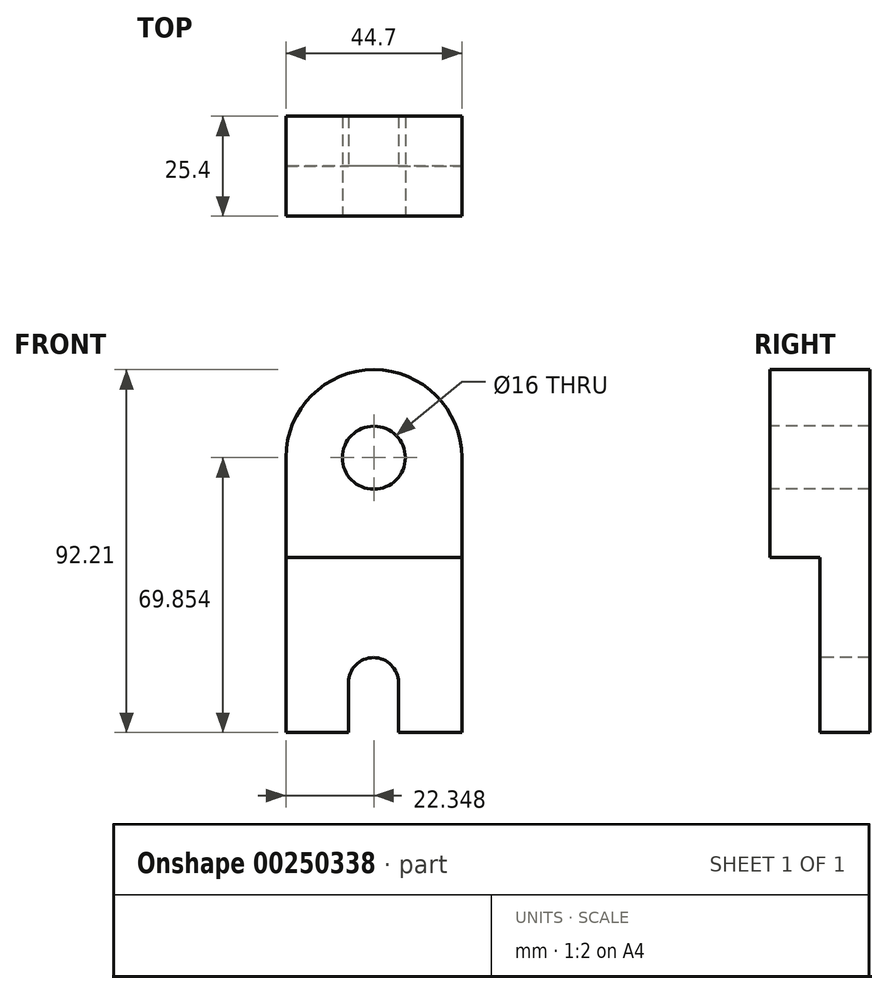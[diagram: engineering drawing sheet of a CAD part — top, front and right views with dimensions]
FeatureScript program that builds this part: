
annotation { "Feature Type Name" : "Feature", "Feature Type Description" : "" }
export const myFeature = defineFeature(function(context is Context, id is Id, definition is map)
    precondition{}
    {
        {
            var Q0;
            Q0=qCreatedBy(makeId("Front.planeOp"),FACE);
            var sketch = newSketch(context, id + "F0", { "sketchPlane" : qUnion([Q0])});
            skLineSegment(sketch, "E0", {"start": v(-44.7, -31.42) * mm, "end": v(-44.7, 38.43) * mm});
            skLineSegment(sketch, "E1", {"start": v(-44.7, -31.42) * mm, "end": v(0, -31.42) * mm});
            skLineSegment(sketch, "E2", {"start": v(0, -31.42) * mm, "end": v(0, 38.43) * mm});
            skArc(sketch, "E3", {"start": v(0, 38.43) * mm, "mid": v(-22.35, 60.79) * mm, "end": v(-44.7, 38.43) * mm});
            skSolve(sketch);
        }
        {
            var Q0;
            Q0=makeQuery(id+"F0.imprint","IMPRINT",FACE,{"disambiguationData":[TD([[makeQuery(id+"F0.imprint","IMPRINT",EDGE,{"derivedFrom":sQuery(id+"F0.wireOp",EDGE,"E0")}),-1.0]])]});
            extrude(context, id + "F1", {"entities" : qUnion([Q0]), "depth" : 25.4 * mm});
        }
        {
            var Q0;
            Q0=makeQuery(id+"F1.opExtrude","CAP_FACE",FACE,{"disambiguationData":[OSD([sQuery(id+"F0.wireOp",EDGE,"E0"),sQuery(id+"F0.wireOp",EDGE,"E1"),sQuery(id+"F0.wireOp",EDGE,"E2"),sQuery(id+"F0.wireOp",EDGE,"E3")])],"isStart":false});
            var sketch = newSketch(context, id + "F2", { "sketchPlane" : qUnion([Q0])});
            skLineSegment(sketch, "E4", {"start": v(-44.7, 38.43) * mm, "end": v(-44.7, 13.03) * mm});
            skLineSegment(sketch, "E5", {"start": v(0, 38.43) * mm, "end": v(0, 13.03) * mm});
            skLineSegment(sketch, "E6", {"start": v(0, 13.03) * mm, "end": v(-44.7, 13.03) * mm});
            skSolve(sketch);
        }
        {
            var Q0;
            {var subQ0=sQuery(id+"F2.wireOp",EDGE,"E6");Q0=makeQuery(id+"F2.imprint","IMPRINT",FACE,{"disambiguationData":[TD([[makeQuery(id+"F2.imprint","IMPRINT",EDGE,{"derivedFrom":subQ0}),1.0]])]});}
            extrude(context, id + "F3", {"entities" : qUnion([Q0]), "operationType" : NewBodyOperationType.REMOVE, "oppositeDirection" : true, "depth" : 12.7 * mm});
        }
        {
            var Q0;
            Q0=makeQuery(id+"F1.opExtrude","CAP_FACE",FACE,{"disambiguationData":[OSD([sQuery(id+"F0.wireOp",EDGE,"E0"),sQuery(id+"F0.wireOp",EDGE,"E1"),sQuery(id+"F0.wireOp",EDGE,"E2"),sQuery(id+"F0.wireOp",EDGE,"E3")])],"isStart":false});
            var sketch = newSketch(context, id + "F4", { "sketchPlane" : qUnion([Q0])});
            skCircle(sketch, "E7", {"center": v(-22.35, 38.43) * mm, "radius": 8 * mm});
            skSolve(sketch);
        }
        {
            var Q0;
            Q0=sQuery(id+"F4.wireOp",VERTEX,"E7.center");
            var Q1;
            Q1=makeQuery(id+"F1.opExtrude","SWEPT_BODY",BODY,{"disambiguationData":[OSD([sQuery(id+"F0.wireOp",EDGE,"E0"),sQuery(id+"F0.wireOp",EDGE,"E1"),sQuery(id+"F0.wireOp",EDGE,"E2"),sQuery(id+"F0.wireOp",EDGE,"E3")])]});
            hole(context, id + "F5", {"style" : HoleStyle.SIMPLE, "endStyle" : HoleEndStyle.THROUGH, "holeDiameter" : 16 * mm, "isTappedThrough" : true, "tappedDepth" : 12.7 * mm, "tapClearance" : 3, "locations" : qUnion([Q0]), "scope" : qUnion([Q1])});
        }
        {
            var Q0;
            Q0=makeQuery(id+"F3.boolean.opBoolean","COPY",FACE,{"derivedFrom":makeQuery(id+"F3.opExtrude","CAP_FACE",FACE,{"disambiguationData":[OSD([sQuery(id+"F0.wireOp",EDGE,"E0"),sQuery(id+"F0.wireOp",EDGE,"E1"),sQuery(id+"F0.wireOp",EDGE,"E2"),sQuery(id+"F2.wireOp",EDGE,"E6")])],"isStart":false})});
            var sketch = newSketch(context, id + "F6", { "sketchPlane" : qUnion([Q0])});
            skLineSegment(sketch, "E8", {"start": v(-28.79, -31.42) * mm, "end": v(-28.79, -18.72) * mm});
            skLineSegment(sketch, "E9", {"start": v(-16.09, -31.42) * mm, "end": v(-16.09, -18.72) * mm});
            skArc(sketch, "E10", {"start": v(-16.09, -18.72) * mm, "mid": v(-22.44, -12.37) * mm, "end": v(-28.79, -18.72) * mm});
            skSolve(sketch);
        }
        {
            var Q0;
            {var subQ0=sQuery(id+"F6.wireOp",EDGE,"E8");Q0=makeQuery(id+"F6.imprint","IMPRINT",FACE,{"disambiguationData":[TD([[makeQuery(id+"F6.imprint","IMPRINT",EDGE,{"derivedFrom":subQ0}),-1.0]])]});}
            extrude(context, id + "F7", {"entities" : qUnion([Q0]), "operationType" : NewBodyOperationType.REMOVE, "oppositeDirection" : true, "depth" : 25.4 * mm});
        }
    });
